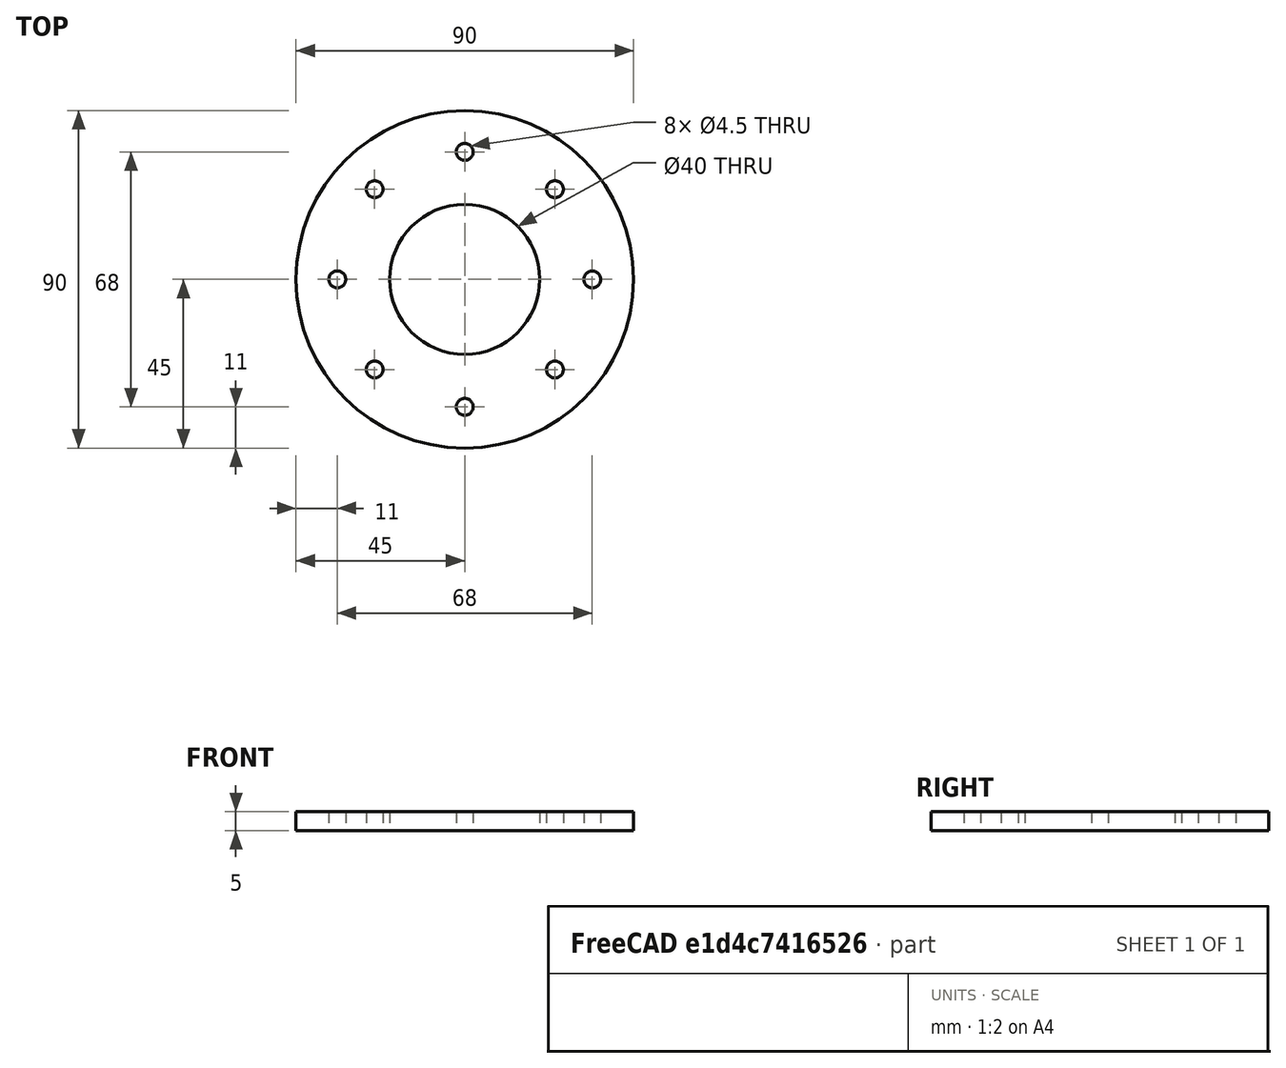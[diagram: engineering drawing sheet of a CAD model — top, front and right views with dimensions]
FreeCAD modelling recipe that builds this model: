
FCSTD DOCUMENT  (FreeCAD 0.18.4R)
Label: Acryl_Ring_spacer_LightDome
License: All rights reserved
LicenseURL: http://en.wikipedia.org/wiki/All_rights_reserved
objects: TechDraw::DrawViewDimension×4, Sketcher::SketchObject×1, Part::Extrusion×1, TechDraw::DrawSVGTemplate×1, TechDraw::DrawViewPart×1, TechDraw::DrawViewAnnotation×1, TechDraw::DrawPage×1
note: 2 computed .brp shape members not serialized (recipe doc carries the construction recipe); baked Part::Feature solids carry a one-line shape summary decoded from their .brp

FEATURE [Sketcher::SketchObject] Sketch
  MapMode = 7
  sketch-geometry (18):
    g0: Circle CenterX=0 CenterY=8e-16 CenterZ=0 NormalX=0 NormalY=0 NormalZ=1 AngleXU=0 Radius=20
    g1: LineSegment [constr] StartX=-70 StartY=70 StartZ=0 EndX=70 EndY=70 EndZ=0
    g2: LineSegment [constr] StartX=70 StartY=70 StartZ=0 EndX=70 EndY=-70 EndZ=0
    g3: LineSegment [constr] StartX=70 StartY=-70 StartZ=0 EndX=-70 EndY=-70 EndZ=0
    g4: LineSegment [constr] StartX=-70 StartY=-70 StartZ=0 EndX=-70 EndY=70 EndZ=0
    g5: LineSegment [constr] StartX=-70 StartY=70 StartZ=0 EndX=70 EndY=-70 EndZ=0
    g6: LineSegment [constr] StartX=70 StartY=70 StartZ=0 EndX=-70 EndY=-70 EndZ=0
    g7: GeomPoint X=0 Y=8e-16 Z=0
    g8: Circle [constr] CenterX=0 CenterY=8e-16 CenterZ=0 NormalX=0 NormalY=0 NormalZ=1 AngleXU=0 Radius=34
    g9: Circle CenterX=0 CenterY=8e-16 CenterZ=0 NormalX=0 NormalY=0 NormalZ=1 AngleXU=0 Radius=45
    g10: Circle CenterX=-24.0416 CenterY=24.0416 CenterZ=0 NormalX=0 NormalY=0 NormalZ=1 AngleXU=0 Radius=2.25
    g11: Circle CenterX=0 CenterY=34 CenterZ=0 NormalX=0 NormalY=0 NormalZ=1 AngleXU=0 Radius=2.25
    g12: Circle CenterX=34 CenterY=0 CenterZ=0 NormalX=0 NormalY=0 NormalZ=1 AngleXU=0 Radius=2.25
    g13: Circle CenterX=0 CenterY=-34 CenterZ=0 NormalX=0 NormalY=0 NormalZ=1 AngleXU=0 Radius=2.25
    g14: Circle CenterX=-24.0416 CenterY=-24.0416 CenterZ=0 NormalX=0 NormalY=0 NormalZ=1 AngleXU=0 Radius=2.25
    g15: Circle CenterX=-34 CenterY=0 CenterZ=0 NormalX=0 NormalY=0 NormalZ=1 AngleXU=0 Radius=2.25
    g16: Circle CenterX=24.0416 CenterY=-24.0416 CenterZ=0 NormalX=0 NormalY=0 NormalZ=1 AngleXU=0 Radius=2.25
    g17: Circle CenterX=24.0416 CenterY=24.0416 CenterZ=0 NormalX=0 NormalY=0 NormalZ=1 AngleXU=0 Radius=2.25
  constraints (49):
    c: Coincident(g0,g-1)
    c: Radius(g0) = 20
    c: Coincident(g1,g2)
    c: Coincident(g2,g3)
    c: Coincident(g3,g4)
    c: Coincident(g4,g1)
    c: Horizontal(g1)
    c: Horizontal(g3)
    c: Vertical(g2)
    c: Vertical(g4)
    c: PointOnObject(g7,g5)
    c: PointOnObject(g7,g6)
    c: Coincident(g6,g1)
    c: Coincident(g5,g1)
    c: Coincident(g6,g3)
    c: Coincident(g5,g2)
    c: Coincident(g7,g0)
    c: Equal(g1,g4)
    c: Equal(g4,g2)
    c: Equal(g2,g3)
    c: DistanceX(g1,g1) = 140
    c: Radius(g8) = 34
    c: Coincident(g8,g0)
    c: Radius(g9) = 45
    c: Coincident(g9,g0)
    c: Radius(g10) = 2.25
    c: PointOnObject(g10,g8)
    c: PointOnObject(g10,g5)
    c: Radius(g11) = 2.25
    c: PointOnObject(g11,g-2)
    c: PointOnObject(g11,g8)
    c: Radius(g17) = 2.25
    c: PointOnObject(g17,g6)
    c: PointOnObject(g17,g8)
    c: Radius(g12) = 2.25
    c: PointOnObject(g12,g-1)
    c: PointOnObject(g12,g8)
    c: Radius(g16) = 2.25
    c: PointOnObject(g16,g5)
    c: PointOnObject(g16,g8)
    c: Radius(g13) = 2.25
    c: PointOnObject(g13,g-2)
    c: PointOnObject(g13,g8)
    c: Radius(g14) = 2.25
    c: PointOnObject(g14,g6)
    c: PointOnObject(g14,g8)
    c: Radius(g15) = 2.25
    c: PointOnObject(g15,g-1)
    c: PointOnObject(g15,g8)
FEATURE [Part::Extrusion] Extrude
  Base = -> Sketch
  Dir = (0,0,1)
  DirMode = 2
  FaceMakerClass = Part::FaceMakerBullseye
  LengthFwd = 5
  LengthRev = 0
  Placement = pos=(0,0,0) rot=(0,0,-1;0.785398rad)
  Solid = true
  Symmetric = false
FEATURE [TechDraw::DrawSVGTemplate] Template
  EditableTexts = AUTHOR_NAME=Norman Rembarz; DN=1; DRAWING_TITLE=Project Regreen Sensolab; FC-DATE=28/10/2020; FC-REV=REV A; FC-SC=1:1; FC-SH=1; FC-SI=A4; FreeCAD_DRAWING=for light-dome module; PN=LAB-LD-SP; SI-1=acrylic spacer; SI-3=REGREEN PROJECT of EU
  Height = 210
  Orientation = 1
  Width = 297
FEATURE [TechDraw::DrawViewPart] View
  CoarseView = false
  Direction = (0,0,0.26)
  Focus = 100
  HardHidden = false
  IsoCount = 0
  IsoHidden = false
  IsoVisible = false
  LockPosition = false
  Perspective = false
  Rotation = 0
  ScaleType = 0
  SeamHidden = false
  SeamVisible = false
  SmoothHidden = false
  SmoothVisible = false
  Source = -> [Extrude]
  X = 146.798
  Y = 117.979
FEATURE [TechDraw::DrawViewDimension] Dimension
  Arbitrary = false
  FormatSpec = ⌀%.2f
  LockPosition = false
  MeasureType = 1
  OverTolerance = 0
  References2D = -> [View]
  Rotation = 0
  ScaleType = 0
  Type = 5
  UnderTolerance = 0
  X = 47.234
  Y = 56.5957
FEATURE [TechDraw::DrawViewDimension] Dimension001
  Arbitrary = false
  FormatSpec = ⌀%.2f
  LockPosition = false
  MeasureType = 1
  OverTolerance = 0
  References2D = -> [View]
  Rotation = 0
  ScaleType = 0
  Type = 5
  UnderTolerance = 0
  X = -77.0213
  Y = 27.234
FEATURE [TechDraw::DrawViewDimension] Dimension002
  Arbitrary = false
  FormatSpec = ⌀%.2f
  LockPosition = false
  MeasureType = 1
  OverTolerance = 0
  References2D = -> [View]
  Rotation = 0
  ScaleType = 0
  Type = 5
  UnderTolerance = 0
  X = -75.9574
  Y = 44.0426
FEATURE [TechDraw::DrawViewAnnotation] Annotation
  Font = osifont
  LineSpace = 80
  LockPosition = false
  MaxWidth = -1
  Rotation = 0
  ScaleType = 0
  Text = thickness of acrylic material | should be 5mm
  TextSize = 5
  TextStyle = 0
  X = 238.5
  Y = 75.6383
FEATURE [TechDraw::DrawViewDimension] Dimension003
  Arbitrary = false
  FormatSpec = %.2f
  LockPosition = false
  MeasureType = 1
  OverTolerance = 0
  References2D = -> [View]
  Rotation = 0
  ScaleType = 0
  Type = 0
  UnderTolerance = 0
  X = 0
  Y = -10.8298
FEATURE [TechDraw::DrawPage] Page
  KeepUpdated = true
  ProjectionType = 0
  Template = -> Template
  Views = -> [View,Dimension,Dimension001,Dimension002,Annotation,Dimension003]
